# Revit family: TESK_Насос вертикальный_SVM(T)-150
name_source: partatom
category: Оборудование
units: mm (PartAtom-declared; Revit-internal decimal feet)

## family parameters
Всегда вертикально = Да
Классификация = Насос
На основе рабочей плоскости = Нет
Общий = Нет
При загрузке вырезать с полостями = Нет
Размер круглого соединителя = Использовать диаметр
Тип детали = Вставляется
Точка расчета площади = Нет

## types (34) — shared parameters
ADSK_Версия Revit = 2019
ADSK_Версия семейства = 1.0
ADSK_Диаметр условный = 125 мм
ADSK_Единица измерения = шт.
ADSK_Завод-изготовитель = TESK
ADSK_Классификация нагрузок = Прочее
ADSK_Количество = 1
ADSK_Количество фаз = 3
ADSK_Количество фаз числовое = 3
ADSK_Коэффициент мощности = 1
ADSK_Наименование краткое = Вертикальный многоступенчатый центробежный насос
ADSK_Напряжение = 400 В
URL = www.teskpump.ru
Материал_1 = TESK_Черный_Условный
Материал_2 = TESK_Нержавеющая сталь
Материал_КорпусДвигателя = TESK_Черный_Ребра_Условный
Таблица_Поиска = TESK_SVM(T)-150
УГО_Длина = 380 мм
Фланец_Толщина = 30 мм

## per-type parameters (varying)
| type | ADSK_Код изделия | ADSK_Масса | ADSK_Масса_Текст | ADSK_Наименование | ADSK_Номинальная мощность | ADSK_Полная мощность | D_Башня | Высота_Башня | Высота_Корпуса | Двигатель_Высота | Двигатель_ОтступКоробки | Двигатель_Ширина | Материал_КорпусУлитка | Напор максимальный | Толщина_ФланцаДвигателя |
| SVM 150-1-1 11kW 3x380V 50Hz IE3 | 77150-10-10003380NSSF | 235 | 235 | Вертикальный многоступенчатый центробежный насос SVM, DN125, PN25-40, Hmax=18.3м (3x380V 50Hz IE3) | 11 кВт | 11 кВ·А | 263 мм | 300 мм | 840 мм | 580 мм | 260 мм | 350 мм | TESK_Нержавеющая сталь | 18.3 | 17 мм |
| SVM 150-1 15kW 3x380V 50Hz IE3 | 77150-100003380NSSF | 235 | 235 | Вертикальный многоступенчатый центробежный насос SVM, DN125, PN25-40, Hmax=24м (3x380V 50Hz IE3) | 15 кВт | 15 кВ·А | 263 мм | 300 мм | 840 мм | 580 мм | 260 мм | 350 мм | TESK_Нержавеющая сталь | 24 | 17 мм |
| SVM 150-2-2 18.5kW 3x380V 50Hz IE3 | 77150-20-20003380NSSF | 250 | 250 | Вертикальный многоступенчатый центробежный насос SVM, DN125, PN25-40, Hmax=37м (3x380V 50Hz IE3) | 19 кВт | 19 кВ·А | 263 мм | 340 мм | 1000 мм | 610 мм | 260 мм | 350 мм | TESK_Нержавеющая сталь | 37 | 18 мм |
| SVM 150-2-1 22kW 3x380V 50Hz IE3 | 77150-20-10003380NSSF | 295 | 295 | Вертикальный многоступенчатый центробежный насос SVM, DN125, PN25-40, Hmax=44.3м (3x380V 50Hz IE3) | 22 кВт | 22 кВ·А | 270 мм | 340 мм | 1000 мм | 645 мм | 285 мм | 360 мм | TESK_Нержавеющая сталь | 44.3 | 19 мм |
| SVM 150-2 30kW 3x380V 50Hz IE3 | 77150-200003380NSSF | 350 | 350 | Вертикальный многоступенчатый центробежный насос SVM, DN125, PN25-40, Hmax=50м (3x380V 50Hz IE3) | 30 кВт | 30 кВ·А | 300 мм | 340 мм | 1000 мм | 705 мм | 310 мм | 400 мм | TESK_Нержавеющая сталь | 50 | 21 мм |
| SVM 150-3-2 30kW 3x380V 50Hz IE3 | 77150-30-20003380NSSF | 360 | 360 | Вертикальный многоступенчатый центробежный насос SVM, DN125, PN25-40, Hmax=63.5м (3x380V 50Hz IE3) | 30 кВт | 30 кВ·А | 300 мм | 380 мм | 1160 мм | 705 мм | 310 мм | 400 мм | TESK_Нержавеющая сталь | 63.5 | 21 мм |
| SVM 150-3-1 37kW 3x380V 50Hz IE3 | 77150-30-10003380NSSF | 385 | 385 | Вертикальный многоступенчатый центробежный насос SVM, DN125, PN25-40, Hmax=70м (3x380V 50Hz IE3) | 37 кВт | 37 кВ·А | 300 мм | 380 мм | 1160 мм | 705 мм | 310 мм | 400 мм | TESK_Нержавеющая сталь | 70 | 21 мм |
| SVM 150-3 37kW 3x380V 50Hz IE3 | 77150-300003380NSSF | 385 | 385 | Вертикальный многоступенчатый центробежный насос SVM, DN125, PN25-40, Hmax=78м (3x380V 50Hz IE3) | 37 кВт | 37 кВ·А | 300 мм | 380 мм | 1160 мм | 705 мм | 310 мм | 400 мм | TESK_Нержавеющая сталь | 78 | 21 мм |
| SVM 150-4-2 45kW 3x380V 50Hz IE3 | 77150-40-20003380NSSF | 460 | 460 | Вертикальный многоступенчатый центробежный насос SVM, DN125, PN25-40, Hmax=89м (3x380V 50Hz IE3) | 45 кВт | 45 кВ·А | 345 мм | 420 мм | 1320 мм | 740 мм | 340 мм | 460 мм | TESK_Нержавеющая сталь | 89 | 22 мм |
| SVM 150-4-1 45kW 3x380V 50Hz IE3 | 77150-40-10003380NSSF | 460 | 460 | Вертикальный многоступенчатый центробежный насос SVM, DN125, PN25-40, Hmax=96.5м (3x380V 50Hz IE3) | 45 кВт | 45 кВ·А | 345 мм | 420 мм | 1320 мм | 740 мм | 340 мм | 460 мм | TESK_Нержавеющая сталь | 96.5 | 22 мм |
| SVM 150-4 55kW 3x380V 50Hz IE3 | 77150-400003380NSSF | 560 | 560 | Вертикальный многоступенчатый центробежный насос SVM, DN125, PN25-40, Hmax=104м (3x380V 50Hz IE3) | 55 кВт | 55 кВ·А | 413 мм | 440 мм | 1350 мм | 810 мм | 370 мм | 550 мм | TESK_Нержавеющая сталь | 104 | 24 мм |
| SVM 150-5-2 55kW 3x380V 50Hz IE3 | 77150-50-20003380NSSF | 570 | 570 | Вертикальный многоступенчатый центробежный насос SVM, DN125, PN25-40, Hmax=115.5м (3x380V 50Hz IE3) | 55 кВт | 55 кВ·А | 413 мм | 500 мм | 1510 мм | 810 мм | 370 мм | 550 мм | TESK_Нержавеющая сталь | 115.5 | 24 мм |
| SVM 150-5-1 75kW 3x380V 50Hz IE3 | 77150-50-10003380NSSF | 690 | 690 | Вертикальный многоступенчатый центробежный насос SVM, DN125, PN25-40, Hmax=122.5м (3x380V 50Hz IE3) | 75 кВт | 75 кВ·А | 435 мм | 500 мм | 1510 мм | 870 мм | 410 мм | 580 мм | TESK_Нержавеющая сталь | 122.5 | 26 мм |
| SVM 150-5 75kW 3x380V 50Hz IE3 | 77150-500003380NSSF | 690 | 690 | Вертикальный многоступенчатый центробежный насос SVM, DN125, PN25-40, Hmax=130м (3x380V 50Hz IE3) | 75 кВт | 75 кВ·А | 435 мм | 500 мм | 1510 мм | 870 мм | 410 мм | 580 мм | TESK_Нержавеющая сталь | 130 | 26 мм |
| SVM 150-6-2 75kW 3x380V 50Hz IE3 | 77150-60-20003380NSSF | 700 | 700 | Вертикальный многоступенчатый центробежный насос SVM, DN125, PN25-40, Hmax=140м (3x380V 50Hz IE3) | 75 кВт | 75 кВ·А | 435 мм | 560 мм | 1670 мм | 870 мм | 410 мм | 580 мм | TESK_Нержавеющая сталь | 140 | 26 мм |
| SVM 150-6-1 75kW 3x380V 50Hz IE3 | 77150-60-10003380NSSF | 703 | 703 | Вертикальный многоступенчатый центробежный насос SVM, DN125, PN25-40, Hmax=148.5м (3x380V 50Hz IE3) | 75 кВт | 75 кВ·А | 435 мм | 560 мм | 1670 мм | 870 мм | 410 мм | 580 мм | TESK_Нержавеющая сталь | 148.5 | 26 мм |
| SVM 150-6 75kW 3x380V 50Hz IE3 | 77150-600003380NSSF | 703 | 703 | Вертикальный многоступенчатый центробежный насос SVM, DN125, PN25-40, Hmax=157м (3x380V 50Hz IE3) | 75 кВт | 75 кВ·А | 435 мм | 560 мм | 1670 мм | 870 мм | 410 мм | 580 мм | TESK_Нержавеющая сталь | 157 | 26 мм |
| SVMT 150-1-1 11kW 3x380V 50Hz IE3 | 77150-10-10003380N | 235 | 235 | Вертикальный многоступенчатый центробежный насос SVMT, DN125, PN25-40, Hmax=18.3м (3x380V 50Hz IE3) | 11 кВт | 11 кВ·А | 263 мм | 300 мм | 840 мм | 580 мм | 260 мм | 350 мм | TESK_Черный_Условный | 18.3 | 17 мм |
| SVMT 150-1 15kW 3x380V 50Hz IE3 | 77150-100003380N | 235 | 235 | Вертикальный многоступенчатый центробежный насос SVMT, DN125, PN25-40, Hmax=24м (3x380V 50Hz IE3) | 15 кВт | 15 кВ·А | 263 мм | 300 мм | 840 мм | 580 мм | 260 мм | 350 мм | TESK_Черный_Условный | 24 | 17 мм |
| SVMT 150-2-2 18.5kW 3x380V 50Hz IE3 | 77150-20-20003380N | 250 | 250 | Вертикальный многоступенчатый центробежный насос SVMT, DN125, PN25-40, Hmax=37м (3x380V 50Hz IE3) | 19 кВт | 19 кВ·А | 263 мм | 340 мм | 1000 мм | 610 мм | 260 мм | 350 мм | TESK_Черный_Условный | 37 | 18 мм |
| SVMT 150-2-1 22kW 3x380V 50Hz IE3 | 77150-20-10003380N | 295 | 295 | Вертикальный многоступенчатый центробежный насос SVMT, DN125, PN25-40, Hmax=44.3м (3x380V 50Hz IE3) | 22 кВт | 22 кВ·А | 270 мм | 340 мм | 1000 мм | 645 мм | 285 мм | 360 мм | TESK_Черный_Условный | 44.3 | 19 мм |
| SVMT 150-2 30kW 3x380V 50Hz IE3 | 77150-200003380N | 350 | 350 | Вертикальный многоступенчатый центробежный насос SVMT, DN125, PN25-40, Hmax=50м (3x380V 50Hz IE3) | 30 кВт | 30 кВ·А | 300 мм | 340 мм | 1000 мм | 705 мм | 310 мм | 400 мм | TESK_Черный_Условный | 50 | 21 мм |
| SVMT 150-3-2 30kW 3x380V 50Hz IE3 | 77150-30-20003380N | 360 | 360 | Вертикальный многоступенчатый центробежный насос SVMT, DN125, PN25-40, Hmax=63.5м (3x380V 50Hz IE3) | 30 кВт | 30 кВ·А | 300 мм | 380 мм | 1160 мм | 705 мм | 310 мм | 400 мм | TESK_Черный_Условный | 63.5 | 21 мм |
| SVMT 150-3-1 37kW 3x380V 50Hz IE3 | 77150-30-10003380N | 385 | 385 | Вертикальный многоступенчатый центробежный насос SVMT, DN125, PN25-40, Hmax=70м (3x380V 50Hz IE3) | 37 кВт | 37 кВ·А | 300 мм | 380 мм | 1160 мм | 705 мм | 310 мм | 400 мм | TESK_Черный_Условный | 70 | 21 мм |
| SVMT 150-3 37kW 3x380V 50Hz IE3 | 77150-300003380N | 385 | 385 | Вертикальный многоступенчатый центробежный насос SVMT, DN125, PN25-40, Hmax=78м (3x380V 50Hz IE3) | 37 кВт | 37 кВ·А | 300 мм | 380 мм | 1160 мм | 705 мм | 310 мм | 400 мм | TESK_Черный_Условный | 78 | 21 мм |
| SVMT 150-4-2 45kW 3x380V 50Hz IE3 | 77150-40-20003380N | 460 | 460 | Вертикальный многоступенчатый центробежный насос SVMT, DN125, PN25-40, Hmax=89м (3x380V 50Hz IE3) | 45 кВт | 45 кВ·А | 345 мм | 420 мм | 1320 мм | 740 мм | 340 мм | 460 мм | TESK_Черный_Условный | 89 | 22 мм |
| SVMT 150-4-1 45kW 3x380V 50Hz IE3 | 77150-40-10003380N | 460 | 460 | Вертикальный многоступенчатый центробежный насос SVMT, DN125, PN25-40, Hmax=96.5м (3x380V 50Hz IE3) | 45 кВт | 45 кВ·А | 345 мм | 420 мм | 1320 мм | 740 мм | 340 мм | 460 мм | TESK_Черный_Условный | 96.5 | 22 мм |
| SVMT 150-4 55kW 3x380V 50Hz IE3 | 77150-400003380N | 560 | 560 | Вертикальный многоступенчатый центробежный насос SVMT, DN125, PN25-40, Hmax=104м (3x380V 50Hz IE3) | 55 кВт | 55 кВ·А | 413 мм | 440 мм | 1350 мм | 810 мм | 370 мм | 550 мм | TESK_Черный_Условный | 104 | 24 мм |
| SVMT 150-5-2 55kW 3x380V 50Hz IE3 | 77150-50-20003380N | 570 | 570 | Вертикальный многоступенчатый центробежный насос SVMT, DN125, PN25-40, Hmax=115.5м (3x380V 50Hz IE3) | 55 кВт | 55 кВ·А | 413 мм | 500 мм | 1510 мм | 810 мм | 370 мм | 550 мм | TESK_Черный_Условный | 115.5 | 24 мм |
| SVMT 150-5-1 75kW 3x380V 50Hz IE3 | 77150-50-10003380N | 690 | 690 | Вертикальный многоступенчатый центробежный насос SVMT, DN125, PN25-40, Hmax=122.5м (3x380V 50Hz IE3) | 75 кВт | 75 кВ·А | 435 мм | 500 мм | 1510 мм | 870 мм | 410 мм | 580 мм | TESK_Черный_Условный | 122.5 | 26 мм |
| SVMT 150-5 75kW 3x380V 50Hz IE3 | 77150-500003380N | 690 | 690 | Вертикальный многоступенчатый центробежный насос SVMT, DN125, PN25-40, Hmax=130м (3x380V 50Hz IE3) | 75 кВт | 75 кВ·А | 435 мм | 500 мм | 1510 мм | 870 мм | 410 мм | 580 мм | TESK_Черный_Условный | 130 | 26 мм |
| SVMT 150-6-2 75kW 3x380V 50Hz IE3 | 77150-60-20003380N | 700 | 700 | Вертикальный многоступенчатый центробежный насос SVMT, DN125, PN25-40, Hmax=140м (3x380V 50Hz IE3) | 75 кВт | 75 кВ·А | 435 мм | 560 мм | 1670 мм | 870 мм | 410 мм | 580 мм | TESK_Черный_Условный | 140 | 26 мм |
| SVMT 150-6-1 75kW 3x380V 50Hz IE3 | 77150-60-10003380N | 703 | 703 | Вертикальный многоступенчатый центробежный насос SVMT, DN125, PN25-40, Hmax=148.5м (3x380V 50Hz IE3) | 75 кВт | 75 кВ·А | 435 мм | 560 мм | 1670 мм | 870 мм | 410 мм | 580 мм | TESK_Черный_Условный | 148.5 | 26 мм |
| SVMT 150-6 75kW 3x380V 50Hz IE3 | 77150-600003380N | 703 | 703 | Вертикальный многоступенчатый центробежный насос SVMT, DN125, PN25-40, Hmax=157м (3x380V 50Hz IE3) | 75 кВт | 75 кВ·А | 435 мм | 560 мм | 1670 мм | 870 мм | 410 мм | 580 мм | TESK_Черный_Условный | 157 | 26 мм |

note: column(s) folded — value = type name in every type: ADSK_Марка
